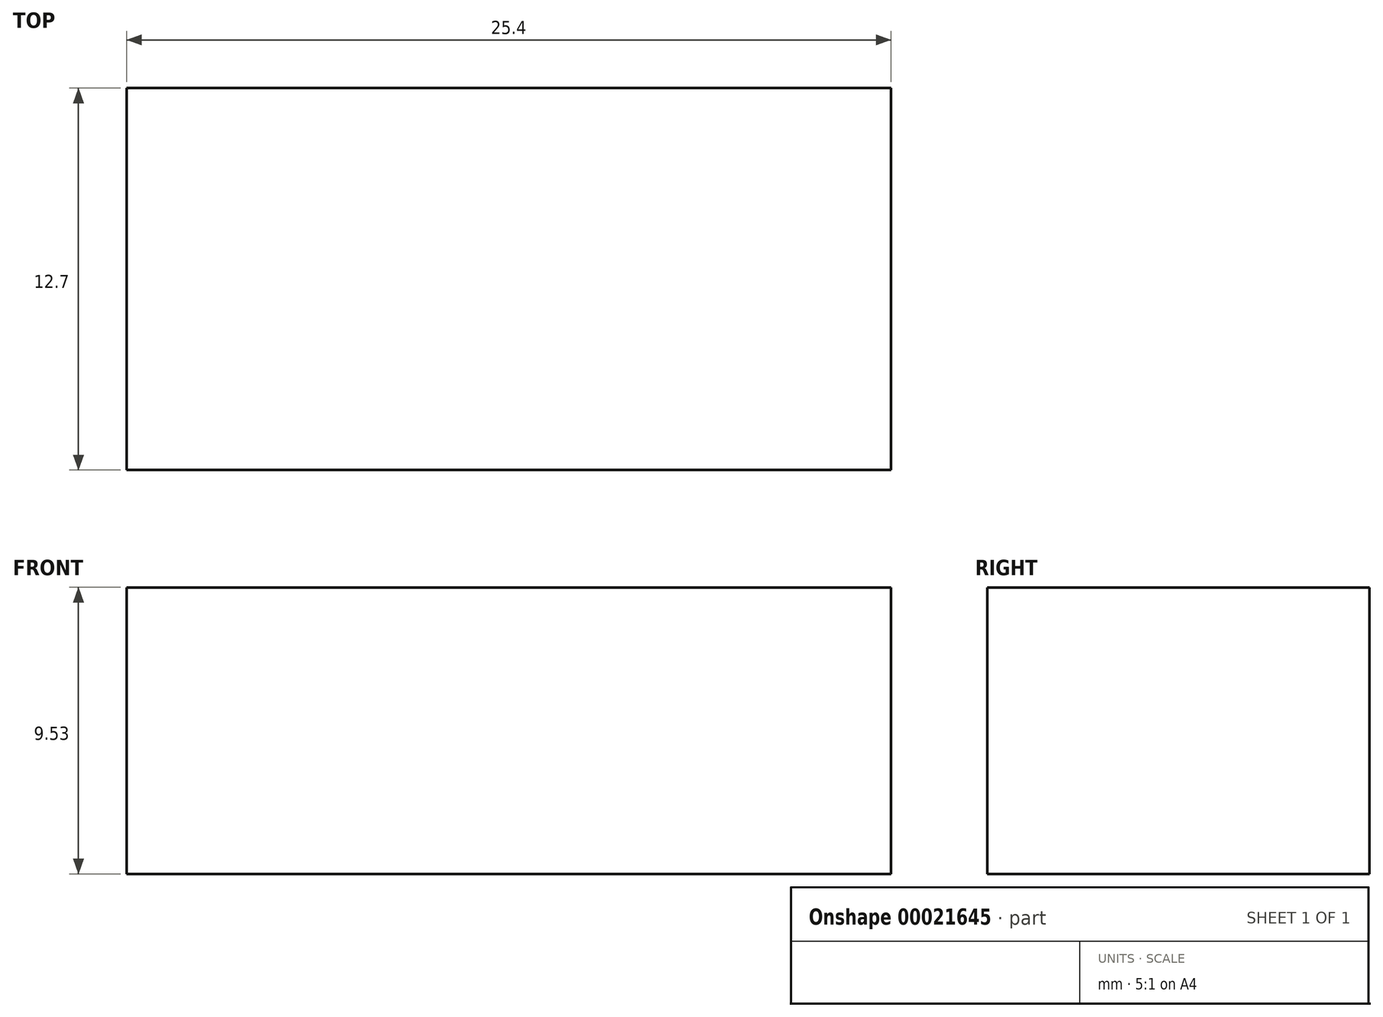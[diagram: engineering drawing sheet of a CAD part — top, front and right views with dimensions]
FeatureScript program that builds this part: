
annotation { "Feature Type Name" : "Feature", "Feature Type Description" : "" }
export const myFeature = defineFeature(function(context is Context, id is Id, definition is map)
    precondition{}
    {
        {
            var Q0;
            Q0=qCreatedBy(makeId("Top.planeOp"),FACE);
            var sketch = newSketch(context, id + "F0", { "sketchPlane" : qUnion([Q0])});
            skLineSegment(sketch, "E0.bottom", {"start": v(-49.66, 12.7) * mm, "end": v(-24.26, 12.7) * mm});
            skLineSegment(sketch, "E0.top", {"start": v(-49.66, 0) * mm, "end": v(-24.26, 0) * mm});
            skLineSegment(sketch, "E0.left", {"start": v(-49.66, 12.7) * mm, "end": v(-49.66, 0) * mm});
            skLineSegment(sketch, "E0.right", {"start": v(-24.26, 12.7) * mm, "end": v(-24.26, 0) * mm});
            skCircle(sketch, "E1", {"center": v(30.7, 22.2) * mm, "radius": 4.76 * mm});
            skSolve(sketch);
        }
        {
            var Q0;
            Q0=makeQuery(id+"F0.imprint","IMPRINT",FACE,{"disambiguationData":[TD([[makeQuery(id+"F0.imprint","IMPRINT",EDGE,{"derivedFrom":sQuery(id+"F0.wireOp",EDGE,"E0.bottom")}),-1.0]])]});
            extrude(context, id + "F1", {"entities" : qUnion([Q0]), "depth" : 9.52 * mm});
        }
        {
            var Q0;
            Q0=sQuery(id+"F0.wireOp",EDGE,"E1");
            extrude(context, id + "F2", {"bodyType" : ToolBodyType.SURFACE, "surfaceEntities" : qUnion([Q0]), "depth" : 69.85 * mm});
        }
    });
